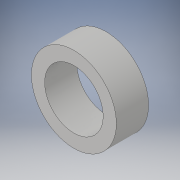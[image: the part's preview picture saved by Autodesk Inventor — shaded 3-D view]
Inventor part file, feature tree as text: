
AUTODESK INVENTOR PART (.ipt)
format: ipt  version: 2019 (Build 230136000, 136)  size: 120,320 bytes
history: native  units: mm
features: other x14, extrude x1, sketch x1
ambient origin geometry x8: Origin, YZ Plane, XZ Plane, XY Plane, X Axis, Y Axis, Z Axis, Center Point
bodies: Solid1 (feature_tree)
feature tree (16):
  extrude  "Extrusion1"  TaperAngle=0.0deg  [1 undecoded]
  other  "to_base_XY"
  other  "to_base_YZ"
  other  "to_base_ZX"
  other  "to_base_X"
  other  "to_base_Y"
  other  "to_base_Z"
  other  "to_base_Center"
  other  "to_nut_XY"
  other  "to_nut_YZ"
  other  "to_nut_ZX"
  other  "to_nut_X"
  other  "to_nut_Y"
  other  "to_nut_Z"
  other  "to_nut_Center"
  sketch  "Sketch_1"  dims[d0=5.5mm d1=0.0mm d2=0.0mm d3=0.0mm]
note: 1 required parameter value undecoded (feature->parameter linkage not recoverable at this tier; creation-order binding heuristic only, values carry confidence <= 0.55)
